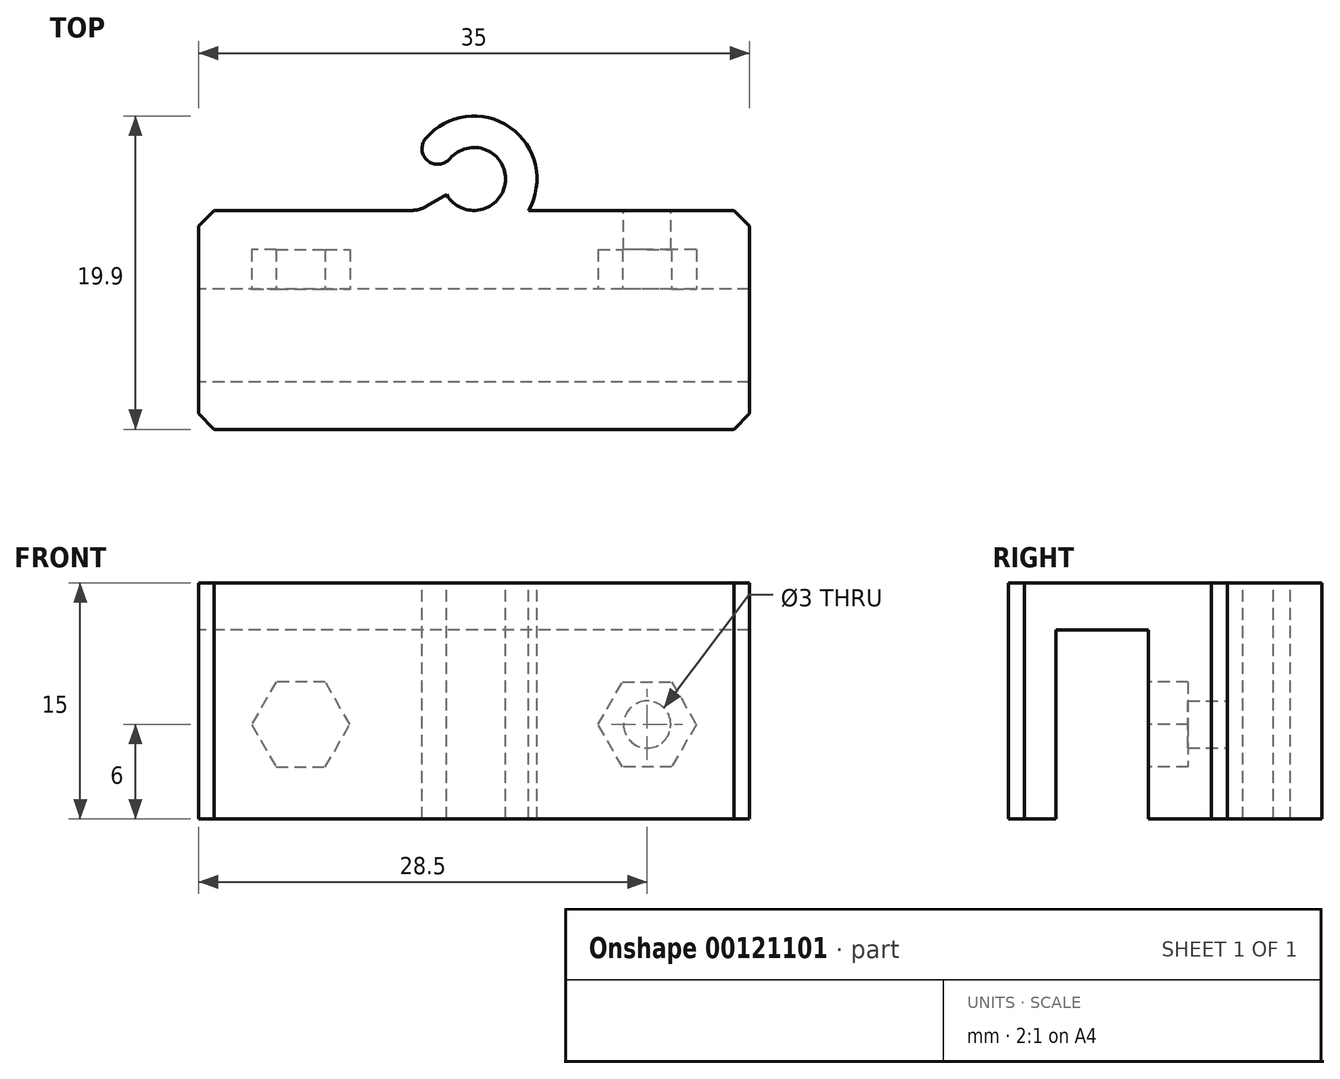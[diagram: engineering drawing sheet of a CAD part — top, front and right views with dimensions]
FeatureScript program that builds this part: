
annotation { "Feature Type Name" : "Feature", "Feature Type Description" : "" }
export const myFeature = defineFeature(function(context is Context, id is Id, definition is map)
    precondition{}
    {
        {
            var Q0;
            Q0=qCreatedBy(makeId("Right.planeOp"),FACE);
            var sketch = newSketch(context, id + "F0", { "sketchPlane" : qUnion([Q0])});
            skLineSegment(sketch, "E0", {"start": v(0, -15) * mm, "end": v(0, 0) * mm});
            skLineSegment(sketch, "E1", {"start": v(0, 0) * mm, "end": v(-13.9, 0) * mm});
            skLineSegment(sketch, "E2", {"start": v(-13.9, 0) * mm, "end": v(-13.9, -15) * mm});
            skLineSegment(sketch, "E3", {"start": v(-13.9, -15) * mm, "end": v(-10.9, -15) * mm});
            skLineSegment(sketch, "E4", {"start": v(-10.9, -15) * mm, "end": v(-10.9, -3) * mm});
            skLineSegment(sketch, "E5", {"start": v(-10.9, -3) * mm, "end": v(-5, -3) * mm});
            skLineSegment(sketch, "E6", {"start": v(-5, -3) * mm, "end": v(-5, -15) * mm});
            skLineSegment(sketch, "E7", {"start": v(-5, -15) * mm, "end": v(0, -15) * mm});
            skSolve(sketch);
        }
        {
            var Q0;
            Q0 = qSketchRegion(id + "F0", true);
            extrude(context, id + "F1", {"entities" : qUnion([Q0]), "endBound" : BoundingType.SYMMETRIC, "depth" : 35 * mm});
        }
        {
            var Q0;
            Q0=makeQuery(id+"F1.opExtrude","SWEPT_FACE",FACE,{"disambiguationData":[OSD([sQuery(id+"F0.wireOp",EDGE,"E1")])]});
            var sketch = newSketch(context, id + "F2", { "sketchPlane" : qUnion([Q0])});
            skCircle(sketch, "E8", {"center": v(0, 2) * mm, "radius": 2 * mm, "construction": true});
            skArc(sketch, "E9", {"start": v(3.46, 0) * mm, "mid": v(2.3, 5.28) * mm, "end": v(-3.06, 4.57) * mm});
            skLineSegment(sketch, "E10", {"start": v(0, 2) * mm, "end": v(-1.53, 3.29) * mm, "construction": true});
            skLineSegment(sketch, "E11", {"start": v(0, 2) * mm, "end": v(-3.46, 0) * mm, "construction": true});
            skLineSegment(sketch, "E12", {"start": v(-3.46, 0) * mm, "end": v(-1.73, 1) * mm});
            skArc(sketch, "E13", {"start": v(-1.53, 3.29) * mm, "mid": v(-2.94, 3.16) * mm, "end": v(-3.06, 4.57) * mm});
            skLineSegment(sketch, "E14", {"start": v(-3.46, 0) * mm, "end": v(3.46, 0) * mm});
            skArc(sketch, "E15", {"start": v(-1.53, 3.29) * mm, "mid": v(2, 1.83) * mm, "end": v(-1.73, 1) * mm});
            skLineSegment(sketch, "E16.trimOffspring", {"start": v(-3.06, 4.57) * mm, "end": v(-6.23, 7.22) * mm, "construction": true});
            skPoint(sketch, "E17.end.orphan", {"position": v(-3.06, 4.57) * mm});
            skSolve(sketch);
        }
        {
            var Q0;
            {var subQ0=sQuery(id+"F2.wireOp",EDGE,"E9");Q0=makeQuery(id+"F2.imprint","IMPRINT",FACE,{"disambiguationData":[TD([[makeQuery(id+"F2.imprint","IMPRINT",EDGE,{"derivedFrom":subQ0}),1.0]])]});}
            var Q1;
            {var subQ0=sQuery(id+"F2.wireOp",EDGE,"E12");Q1=makeQuery(id+"F2.imprint","IMPRINT",FACE,{"disambiguationData":[TD([[makeQuery(id+"F2.imprint","IMPRINT",EDGE,{"derivedFrom":subQ0}),-1.0]])]});}
            extrude(context, id + "F3", {"entities" : qUnion([Q0, Q1]), "operationType" : NewBodyOperationType.ADD, "oppositeDirection" : true, "depth" : 15 * mm});
        }
        {
            var Q0;
            Q0=makeQuery(id+"F3.opExtrude","SWEPT_EDGE",EDGE,{"disambiguationData":[OSD([sQuery(id+"F0.wireOp",EDGE,"E0"),sQuery(id+"F0.wireOp",EDGE,"E1"),sQuery(id+"F2.wireOp",EDGE,"E9"),sQuery(id+"F2.wireOp",EDGE,"E14")])]});
            var Q1;
            Q1=makeQuery(id+"F3.opExtrude","SWEPT_EDGE",EDGE,{"disambiguationData":[OSD([sQuery(id+"F0.wireOp",EDGE,"E0"),sQuery(id+"F0.wireOp",EDGE,"E1"),sQuery(id+"F2.wireOp",EDGE,"E12"),sQuery(id+"F2.wireOp",EDGE,"E14")])]});
            fillet(context, id + "F4", {"entities" : qUnion([Q0, Q1]), "radius" : 2 * mm, "tangentPropagation" : true, "allowEdgeOverflow" : false});
        }
        {
            var Q0;
            Q0=makeQuery(id+"F1.opExtrude","CAP_EDGE",EDGE,{"disambiguationData":[OSD([sQuery(id+"F0.wireOp",EDGE,"E0")])],"isStart":true});
            var Q1;
            Q1=makeQuery(id+"F1.opExtrude","CAP_EDGE",EDGE,{"disambiguationData":[OSD([sQuery(id+"F0.wireOp",EDGE,"E0")])],"isStart":false});
            var Q2;
            Q2=makeQuery(id+"F1.opExtrude","CAP_EDGE",EDGE,{"disambiguationData":[OSD([sQuery(id+"F0.wireOp",EDGE,"E2")])],"isStart":true});
            var Q3;
            Q3=makeQuery(id+"F1.opExtrude","CAP_EDGE",EDGE,{"disambiguationData":[OSD([sQuery(id+"F0.wireOp",EDGE,"E2")])],"isStart":false});
            chamfer(context, id + "F5", {"entities" : qUnion([Q0, Q1, Q2, Q3]), "width" : 1 * mm, "tangentPropagation" : true});
        }
        {
            var Q0;
            Q0=makeQuery(id+"F1.opExtrude","SWEPT_FACE",FACE,{"disambiguationData":[OSD([sQuery(id+"F0.wireOp",EDGE,"E6")])]});
            var sketch = newSketch(context, id + "F6", { "sketchPlane" : qUnion([Q0])});
            skLineSegment(sketch, "E18", {"start": v(14.38, -9) * mm, "end": v(-14.16, -9) * mm, "construction": true});
            skPoint(sketch, "E18.startSnap0", {"position": v(17.5, -9) * mm});
            skCircle(sketch, "E19.cCircle", {"center": v(11, -9) * mm, "radius": 2.7 * mm, "construction": true});
            skLineSegment(sketch, "E19.0", {"start": v(12.56, -11.7) * mm, "end": v(9.44, -11.7) * mm});
            skLineSegment(sketch, "E19.1", {"start": v(9.44, -11.7) * mm, "end": v(7.88, -9) * mm});
            skLineSegment(sketch, "E19.2", {"start": v(7.88, -9) * mm, "end": v(9.44, -6.3) * mm});
            skLineSegment(sketch, "E19.3", {"start": v(9.44, -6.3) * mm, "end": v(12.56, -6.3) * mm});
            skLineSegment(sketch, "E19.4", {"start": v(12.56, -6.3) * mm, "end": v(14.12, -9) * mm});
            skLineSegment(sketch, "E19.5", {"start": v(14.12, -9) * mm, "end": v(12.56, -11.7) * mm});
            skPoint(sketch, "E19.0.midPoint", {"position": v(11, -11.7) * mm});
            skLineSegment(sketch, "E20.MirrorCS", {"start": v(-9.44, -11.7) * mm, "end": v(-7.88, -9) * mm});
            skLineSegment(sketch, "E21.MirrorCS", {"start": v(-12.56, -11.7) * mm, "end": v(-9.44, -11.7) * mm});
            skLineSegment(sketch, "E22.MirrorCS", {"start": v(-14.12, -9) * mm, "end": v(-12.56, -11.7) * mm});
            skLineSegment(sketch, "E23.MirrorCS", {"start": v(-12.56, -6.3) * mm, "end": v(-14.12, -9) * mm});
            skLineSegment(sketch, "E24.MirrorCS", {"start": v(-9.44, -6.3) * mm, "end": v(-12.56, -6.3) * mm});
            skLineSegment(sketch, "E25.MirrorCS", {"start": v(-7.88, -9) * mm, "end": v(-9.44, -6.3) * mm});
            skSolve(sketch);
        }
        {
            var Q0;
            Q0=makeQuery(id+"F6.imprint","IMPRINT",FACE,{"disambiguationData":[TD([[makeQuery(id+"F6.imprint","IMPRINT",EDGE,{"derivedFrom":sQuery(id+"F6.wireOp",EDGE,"E20.MirrorCS")}),1.0]])]});
            var Q1;
            Q1=makeQuery(id+"F6.imprint","IMPRINT",FACE,{"disambiguationData":[TD([[makeQuery(id+"F6.imprint","IMPRINT",EDGE,{"derivedFrom":sQuery(id+"F6.wireOp",EDGE,"E19.0")}),-1.0]])]});
            extrude(context, id + "F7", {"entities" : qUnion([Q0, Q1]), "operationType" : NewBodyOperationType.REMOVE, "oppositeDirection" : true, "depth" : 2.5 * mm});
        }
        {
            var Q0;
            {var subQ0=sQuery(id+"F2.wireOp",EDGE,"E9");var subQ6=sQuery(id+"F0.wireOp",EDGE,"E0");Q0=makeQuery(id+"F3.boolean.opBoolean","SPLIT",FACE,{"disambiguationData":[TD([makeQuery(id+"F3.opExtrude","SWEPT_FACE",FACE,{"disambiguationData":[OSD([subQ0])]})])],"derivedFrom":makeQuery(id+"F1.opExtrude","SWEPT_FACE",FACE,{"disambiguationData":[OSD([subQ6])]})});}
            var sketch = newSketch(context, id + "F8", { "sketchPlane" : qUnion([Q0])});
            skPoint(sketch, "E26.0", {"position": v(-11, -9) * mm});
            skCircle(sketch, "E27", {"center": v(-11, -9) * mm, "radius": 1.5 * mm});
            skCircle(sketch, "E28.MirrorC", {"center": v(11, -9) * mm, "radius": 1.5 * mm});
            skSolve(sketch);
        }
        {
            var Q0;
            Q0=makeQuery(id+"F8.imprint","IMPRINT",FACE,{"disambiguationData":[TD([[makeQuery(id+"F8.imprint","IMPRINT",EDGE,{"derivedFrom":sQuery(id+"F8.wireOp",EDGE,"E27")}),1.0]])]});
            var Q1;
            Q1=makeQuery(id+"F8.imprint","IMPRINT",FACE,{"disambiguationData":[TD([[makeQuery(id+"F8.imprint","IMPRINT",EDGE,{"derivedFrom":sQuery(id+"F8.wireOp",EDGE,"E28.MirrorC")}),-1.0]])]});
            var Q2;
            Q2=makeQuery(id+"F7.boolean.opBoolean","COPY",FACE,{"derivedFrom":makeQuery(id+"F7.opExtrude","CAP_FACE",FACE,{"disambiguationData":[OSD([sQuery(id+"F6.wireOp",EDGE,"E19.0"),sQuery(id+"F6.wireOp",EDGE,"E19.1"),sQuery(id+"F6.wireOp",EDGE,"E19.2"),sQuery(id+"F6.wireOp",EDGE,"E19.3"),sQuery(id+"F6.wireOp",EDGE,"E19.4"),sQuery(id+"F6.wireOp",EDGE,"E19.5")])],"isStart":false})});
            extrude(context, id + "F9", {"entities" : qUnion([Q0, Q1]), "operationType" : NewBodyOperationType.REMOVE, "endBound" : BoundingType.UP_TO_SURFACE, "oppositeDirection" : true, "endBoundEntityFace" : qUnion([Q2]), "depth" : 3 * mm});
        }
    });
